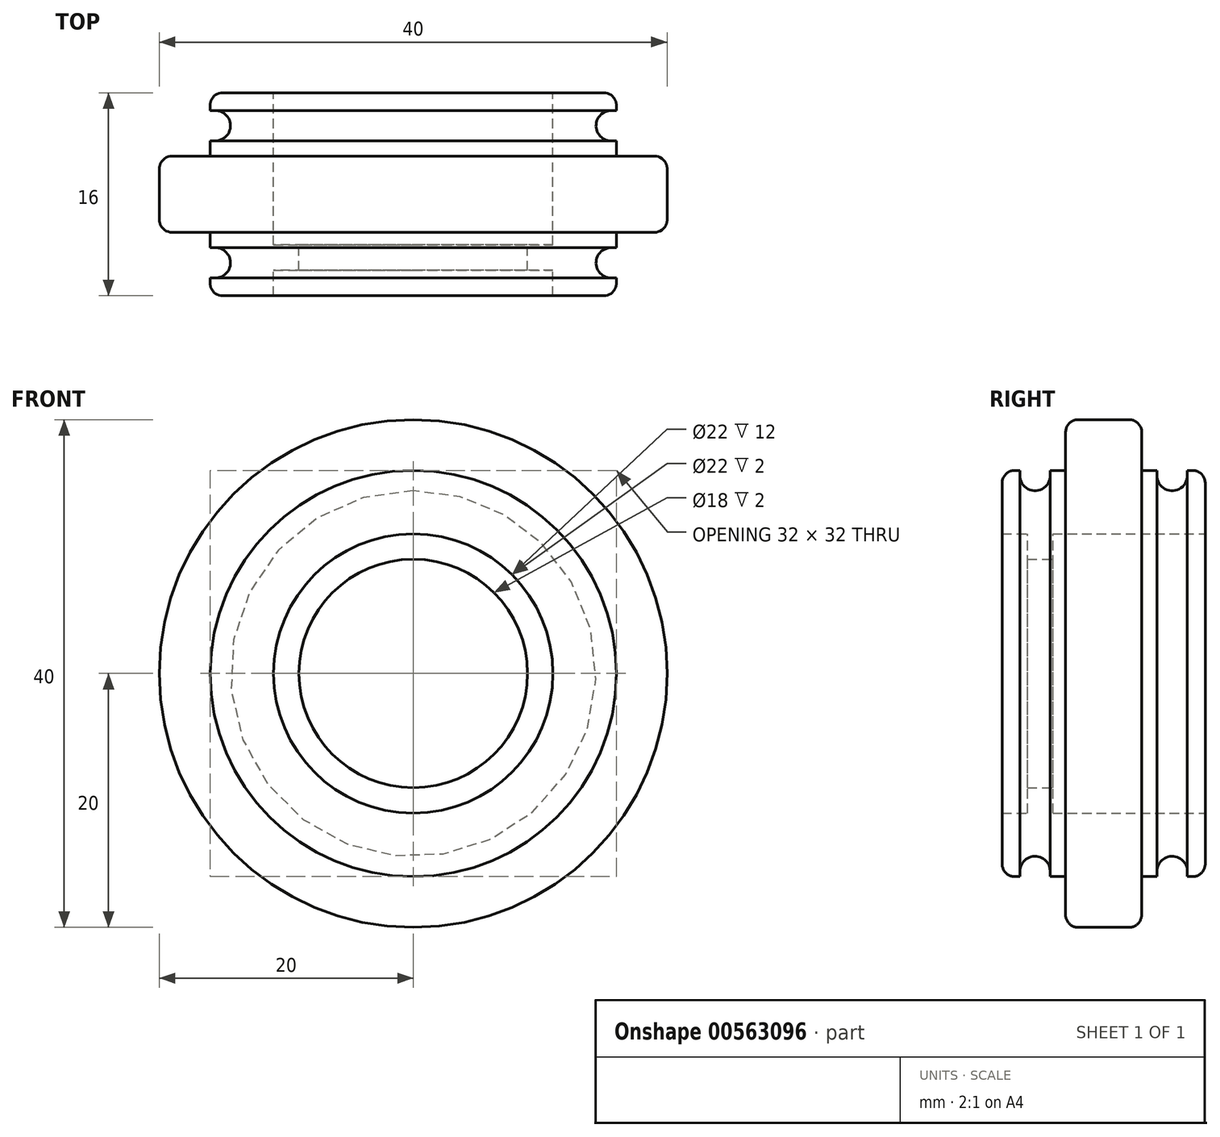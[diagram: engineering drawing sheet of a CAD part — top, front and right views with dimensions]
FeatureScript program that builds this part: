
annotation { "Feature Type Name" : "Feature", "Feature Type Description" : "" }
export const myFeature = defineFeature(function(context is Context, id is Id, definition is map)
    precondition{}
    {
        {
            var Q0;
            Q0=qCreatedBy(makeId("Front.planeOp"),FACE);
            var sketch = newSketch(context, id + "F0", { "sketchPlane" : qUnion([Q0])});
            skCircle(sketch, "E0", {"center": v(0, 0) * mm, "radius": 20 * mm});
            skCircle(sketch, "E1", {"center": v(0, 0) * mm, "radius": 16 * mm});
            skCircle(sketch, "E2", {"center": v(0, 0) * mm, "radius": 11 * mm});
            skCircle(sketch, "E3", {"center": v(0, 0) * mm, "radius": 9 * mm});
            skSolve(sketch);
        }
        {
            var Q0;
            Q0=makeQuery(id+"F0.imprint","IMPRINT",FACE,{"disambiguationData":[TD([[makeQuery(id+"F0.imprint","IMPRINT",EDGE,{"derivedFrom":sQuery(id+"F0.wireOp",EDGE,"E1")}),1.0]])]});
            extrude(context, id + "F1", {"entities" : qUnion([Q0]), "depth" : 8 * mm, "offsetDistance" : 25 * mm, "hasSecondDirection" : true, "secondDirectionOppositeDirection" : true, "secondDirectionDepth" : 8 * mm});
        }
        {
            var Q0;
            Q0=makeQuery(id+"F0.imprint","IMPRINT",FACE,{"disambiguationData":[TD([[makeQuery(id+"F0.imprint","IMPRINT",EDGE,{"derivedFrom":sQuery(id+"F0.wireOp",EDGE,"E0")}),1.0]])]});
            extrude(context, id + "F2", {"entities" : qUnion([Q0]), "operationType" : NewBodyOperationType.ADD, "depth" : 3 * mm, "offsetDistance" : 25 * mm, "hasSecondDirection" : true, "secondDirectionOppositeDirection" : true, "secondDirectionDepth" : 3 * mm});
        }
        {
            var Q0;
            Q0=makeQuery(id+"F2.opExtrude","CAP_EDGE",EDGE,{"disambiguationData":[OSD([sQuery(id+"F0.wireOp",EDGE,"E0")])],"isStart":false});
            var Q1;
            Q1=makeQuery(id+"F2.opExtrude","CAP_EDGE",EDGE,{"disambiguationData":[OSD([sQuery(id+"F0.wireOp",EDGE,"E0")])],"isStart":true});
            var Q2;
            Q2=makeQuery(id+"F1.opExtrude","CAP_EDGE",EDGE,{"disambiguationData":[OSD([sQuery(id+"F0.wireOp",EDGE,"E1")])],"isStart":false});
            var Q3;
            Q3=makeQuery(id+"F1.opExtrude","CAP_EDGE",EDGE,{"disambiguationData":[OSD([sQuery(id+"F0.wireOp",EDGE,"E1")])],"isStart":true});
            fillet(context, id + "F3", {"entities" : qUnion([Q0, Q1, Q2, Q3]), "radius" : 1 * mm, "tangentPropagation" : true, "allowEdgeOverflow" : false});
        }
        {
            var Q0;
            Q0=makeQuery(id+"F0.imprint","IMPRINT",FACE,{"disambiguationData":[TD([[makeQuery(id+"F0.imprint","IMPRINT",EDGE,{"derivedFrom":sQuery(id+"F0.wireOp",EDGE,"E2")}),1.0]])]});
            extrude(context, id + "F4", {"entities" : qUnion([Q0]), "operationType" : NewBodyOperationType.ADD, "depth" : 6 * mm, "offsetDistance" : 25 * mm, "hasSecondDirection" : true, "secondDirectionOppositeDirection" : false, "secondDirectionDepth" : 4 * mm});
        }
        {
            var Q0;
            Q0=qCreatedBy(makeId("Right.planeOp"),FACE);
            var sketch = newSketch(context, id + "F5", { "sketchPlane" : qUnion([Q0])});
            skLineSegment(sketch, "E4", {"start": v(0, 0) * mm, "end": v(-8, 0) * mm, "construction": true});
            skLineSegment(sketch, "E5", {"start": v(-8, 0) * mm, "end": v(-8, 16) * mm, "construction": true});
            skLineSegment(sketch, "E6", {"start": v(-8, 16) * mm, "end": v(-5.5, 16) * mm, "construction": true});
            skLineSegment(sketch, "E7", {"start": v(-4.2, 16.2) * mm, "end": v(-4.2, 22.18) * mm});
            skLineSegment(sketch, "E8", {"start": v(-4.2, 22.18) * mm, "end": v(0, 22.18) * mm});
            skLineSegment(sketch, "E9", {"start": v(-6.5, 16) * mm, "end": v(-12.97, 16) * mm});
            skLineSegment(sketch, "E10", {"start": v(-12.97, 16) * mm, "end": v(-12.97, 0) * mm});
            skLineSegment(sketch, "E11", {"start": v(-12.97, 0) * mm, "end": v(-17.36, 0) * mm});
            skLineSegment(sketch, "E12", {"start": v(-17.36, 0) * mm, "end": v(-17.36, 23.62) * mm});
            skLineSegment(sketch, "E13", {"start": v(-17.36, 23.62) * mm, "end": v(0, 23.62) * mm});
            skLineSegment(sketch, "E14", {"start": v(-6.6, 16) * mm, "end": v(-6.6, 15.6) * mm});
            skLineSegment(sketch, "E15", {"start": v(-6.6, 15.6) * mm, "end": v(-4.2, 15.6) * mm, "construction": true});
            skLineSegment(sketch, "E16", {"start": v(-4.2, 15.6) * mm, "end": v(-4.2, 16.2) * mm});
            skArc(sketch, "E17", {"start": v(-6.6, 15.6) * mm, "mid": v(-5.4, 14.4) * mm, "end": v(-4.2, 15.6) * mm});
            skLineSegment(sketch, "E18.MirrorCS", {"start": v(12.97, 16) * mm, "end": v(12.97, 0) * mm});
            skLineSegment(sketch, "E19.MirrorCS", {"start": v(12.97, 0) * mm, "end": v(17.36, 0) * mm});
            skLineSegment(sketch, "E20.MirrorCS", {"start": v(17.36, 0) * mm, "end": v(17.36, 23.62) * mm});
            skLineSegment(sketch, "E21.MirrorCS", {"start": v(17.36, 23.62) * mm, "end": v(0, 23.62) * mm});
            skLineSegment(sketch, "E22.MirrorCS", {"start": v(4.2, 22.18) * mm, "end": v(0, 22.18) * mm});
            skLineSegment(sketch, "E23.MirrorCS", {"start": v(4.2, 16.2) * mm, "end": v(4.2, 22.18) * mm});
            skLineSegment(sketch, "E24.MirrorCS", {"start": v(6.5, 16) * mm, "end": v(12.97, 16) * mm});
            skArc(sketch, "E25.MirrorCS", {"start": v(6.6, 15.6) * mm, "mid": v(5.4, 14.4) * mm, "end": v(4.2, 15.6) * mm});
            skLineSegment(sketch, "E26.MirrorCS", {"start": v(6.6, 16) * mm, "end": v(6.6, 15.6) * mm});
            skLineSegment(sketch, "E27.MirrorCS", {"start": v(4.2, 15.6) * mm, "end": v(4.2, 16.2) * mm});
            skSolve(sketch);
        }
        {
            var Q0;
            Q0=makeQuery(id+"F5.imprint","IMPRINT",FACE,{"disambiguationData":[TD([[makeQuery(id+"F5.imprint","IMPRINT",EDGE,{"derivedFrom":sQuery(id+"F5.wireOp",EDGE,"E7")}),1.0]])]});
            var Q1;
            Q1=sQuery(id+"F5.wireOp",EDGE,"E19.MirrorCS");
            revolve(context, id + "F6", {"operationType" : NewBodyOperationType.REMOVE, "surfaceOperationType" : NewSurfaceOperationType.NEW, "entities" : qUnion([Q0]), "axis" : qUnion([Q1]), "revolveType" : RevolveType.FULL, "oppositeDirection" : true});
        }
    });
